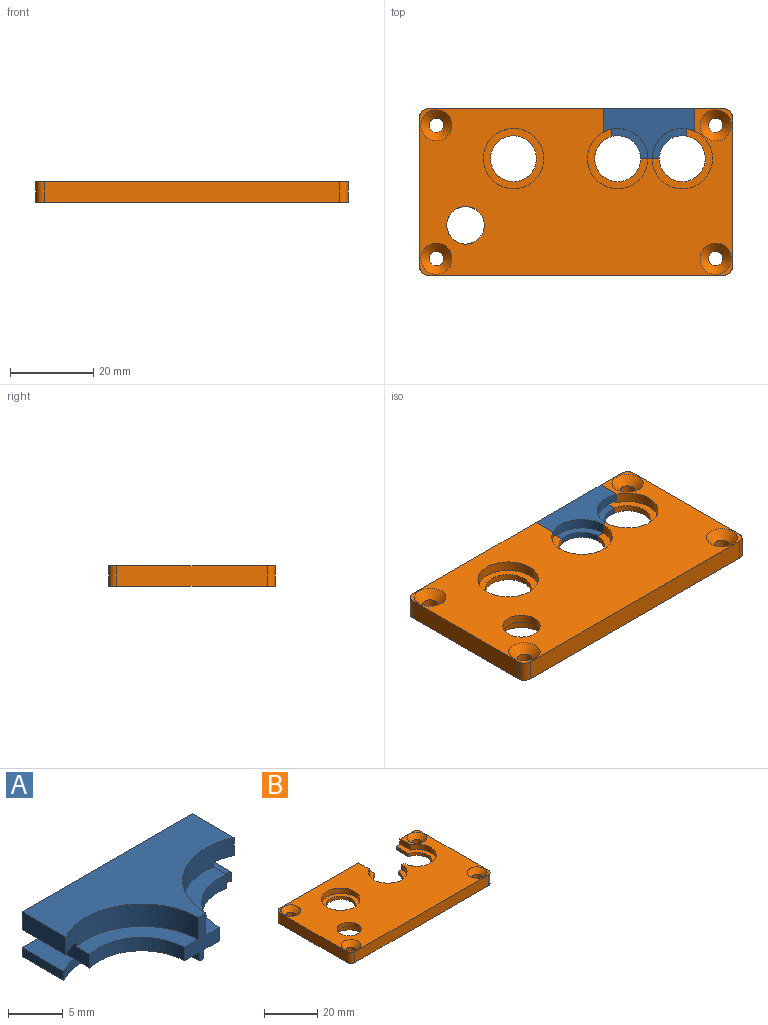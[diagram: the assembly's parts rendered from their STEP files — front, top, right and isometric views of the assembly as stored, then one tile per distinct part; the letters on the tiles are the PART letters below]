
ASSEMBLY  parts=2 mates=1
PART A: 24 faces, bbox 22x12x5 mm
  f0: plane 5x4.5mm, normal (0,-1,0), area 9.7mm2, adj f2,f3,f4,f9,f16,f17,f18,f19
  f1: plane 5.13x1mm, normal (1,0,0), area 5.1mm2, adj f2,f7,f10,f20
  f2: plane 22x12mm, normal (0,0,-1), area 128.5mm2, adj f0,f1,f7,f8,f20,f22
  f3: cylinder r=5.5mm len=6.9mm, axis (0,0,1), area 15.1mm2, adj f0,f15,f17,f23
  f4: cylinder r=5.5mm len=6.4mm, axis (0,0,1), area 14.3mm2, adj f0,f12,f19,f21
  f5: plane 5.65x2mm, normal (-1,0,0), area 11.3mm2, adj f7,f9,f14,f16
  f6: plane 5.4x2mm, normal (1,0,0), area 10.8mm2, adj f7,f9,f11,f18
  f7: plane 22x5mm, normal (0,1,0), area 101.6mm2, adj f1,f2,f5,f6,f8,f9,f10,f11
  f8: plane 5.37x1mm, normal (-1,0,0), area 5.4mm2, adj f2,f7,f13,f22
  f9: plane 22x12mm, normal (0,0,1), area 136mm2, adj f0,f5,f6,f7,f16,f18
  f10: plane 5.13x2.1mm, normal (0,0,1), area 10mm2, adj f1,f7,f12,f20
  f11: plane 5.4x2.1mm, normal (0,0,-1), area 10.6mm2, adj f6,f7,f12,f18
  f12: plane 6.57x2mm, normal (1,0,0), area 12.3mm2, adj f4,f7,f10,f11,f18,f19,f21
  f13: plane 5.37x2.1mm, normal (0,0,1), area 10.4mm2, adj f7,f8,f15,f22
  f14: plane 5.65x2.1mm, normal (0,0,-1), area 10.9mm2, adj f5,f7,f15,f16
  f15: plane 6.68x2mm, normal (-1,0,0), area 12.5mm2, adj f3,f7,f13,f14,f16,f17,f23
  f16: cylinder r=7.25mm len=10.75mm, axis (0,0,1), area 36.5mm2, adj f0,f5,f9,f14,f15,f17
  f17: plane 8.65x7.25mm, normal (0,0,1), area 20mm2, adj f0,f3,f15,f16
  f18: cylinder r=7.25mm len=10.25mm, axis (0,0,1), area 35.1mm2, adj f0,f6,f9,f11,f12,f19
  f19: plane 8.15x7.25mm, normal (0,0,1), area 19.1mm2, adj f0,f4,f12,f18
  f20: cylinder r=7.5mm len=10.5mm, axis (0,0,-1), area 14.9mm2, adj f0,f1,f2,f10,f21
  f21: plane 8.4x7.5mm, normal (0,0,-1), area 22.2mm2, adj f0,f4,f12,f20
  f22: cylinder r=7.5mm len=11mm, axis (0,0,-1), area 15.4mm2, adj f0,f2,f8,f13,f23
  f23: plane 8.9x7.5mm, normal (0,0,-1), area 23.2mm2, adj f0,f3,f15,f22
PART B: 44 faces, bbox 75x40x5 mm
  f0: plane 6.59x1.5mm, normal (-1,0,0), area 9.9mm2, adj f5,f6,f27,f38
  f1: plane 5.4x2.5mm, normal (-1,0,0), area 13.5mm2, adj f5,f17,f27,f28
  f2: plane 5.13x1mm, normal (-1,0,0), area 5.1mm2, adj f5,f18,f37,f38
  f3: plane 5.37x1mm, normal (1,0,0), area 5.4mm2, adj f13,f18,f35,f36
  f4: plane 5.65x2.5mm, normal (1,0,0), area 14.1mm2, adj f13,f17,f29,f30
  f5: plane 9x5mm, normal (0,1,0), area 38mm2, adj f0,f1,f2,f12,f17,f18,f27,f38
  f6: cylinder r=5.5mm len=11mm, axis (0,0,1), area 37.4mm2, adj f0,f27,f38,f42
  f7: cylinder r=5.5mm len=11mm, axis (0,0,1), area 36.6mm2, adj f29,f36,f42,f43
  f8: cylinder r=5.5mm len=11mm, axis (0,0,1), area 51.8mm2, adj f31,f34
  f9: plane 71x5mm, normal (0,-1,0), area 355mm2, adj f10,f16,f17,f18
  f10: cylinder r=2mm len=5mm, axis (0,0,1), area 15.7mm2, adj f9,f11,f17,f18
  f11: plane 36x5mm, normal (1,0,0), area 180mm2, adj f10,f12,f17,f18
  f12: cylinder r=2mm len=5mm, axis (0,0,1), area 15.7mm2, adj f5,f11,f17,f18
  f13: plane 44x5mm, normal (0,1,0), area 213mm2, adj f3,f4,f14,f17,f18,f29,f36,f43
  f14: cylinder r=2mm len=5mm, axis (0,0,1), area 15.7mm2, adj f13,f15,f17,f18
  f15: plane 36x5mm, normal (-1,0,0), area 180mm2, adj f14,f16,f17,f18
  f16: cylinder r=2mm len=5mm, axis (0,0,1), area 15.7mm2, adj f9,f15,f17,f18
  f17: plane 75x40mm, normal (0,0,1), area 2124.9mm2, adj f1,f4,f5,f9,f10,f11,f12,f13
  f18: plane 75x40mm, normal (0,0,-1), area 2166.7mm2, adj f2,f3,f5,f9,f10,f11,f12,f13
  f19: cylinder r=1.75mm len=3.5mm, axis (0,0,1), area 33mm2, adj f18,f26
  f20: cylinder r=1.75mm len=3.5mm, axis (0,0,1), area 33mm2, adj f18,f25
  f21: cylinder r=1.75mm len=3.5mm, axis (0,0,1), area 33mm2, adj f18,f24
  f22: cylinder r=1.75mm len=3.5mm, axis (0,0,1), area 33mm2, adj f18,f23
  f23: cone r=1.75mm half-angle=45deg, axis (0,0,1), area 48.9mm2, adj f17,f22
  f24: cone r=1.75mm half-angle=45deg, axis (0,0,1), area 48.9mm2, adj f17,f21
  f25: cone r=1.75mm half-angle=45deg, axis (0,0,1), area 48.9mm2, adj f17,f20
  f26: cone r=1.75mm half-angle=45deg, axis (0,0,1), area 48.9mm2, adj f17,f19
  f27: plane 19.25x14.5mm, normal (0,0,1), area 60.9mm2, adj f0,f1,f5,f6,f28,f42
  f28: cylinder r=7.25mm len=14.5mm, axis (0,0,1), area 77.7mm2, adj f1,f17,f27,f42
  f29: plane 19.25x14.5mm, normal (0,0,1), area 60.4mm2, adj f4,f7,f13,f30,f42,f43
  f30: cylinder r=7.25mm len=14.5mm, axis (0,0,1), area 76.3mm2, adj f4,f17,f29,f42
  f31: plane 14.5x14.5mm, normal (0,0,1), area 70.1mm2, adj f8,f32
  f32: cylinder r=7.25mm len=14.5mm, axis (0,0,1), area 113.9mm2, adj f17,f31
  f33: cylinder r=7.5mm len=15mm, axis (0,0,-1), area 47.1mm2, adj f18,f34
  f34: plane 15x15mm, normal (0,0,-1), area 81.7mm2, adj f8,f33
  f35: cylinder r=7.5mm len=15mm, axis (0,0,-1), area 31.7mm2, adj f3,f18,f36,f42
  f36: plane 19.5x15mm, normal (0,0,-1), area 68.1mm2, adj f3,f7,f13,f35,f42,f43
  f37: cylinder r=7.5mm len=15mm, axis (0,0,-1), area 32.3mm2, adj f2,f18,f38,f42
  f38: plane 19.5x15mm, normal (0,0,-1), area 68.8mm2, adj f0,f2,f5,f6,f37,f42
  f39: cylinder r=4.5mm len=9mm, axis (0,0,-1), area 56.5mm2, adj f17,f40
  f40: plane 13x13mm, normal (0,0,-1), area 69.1mm2, adj f39,f41
  f41: cylinder r=6.5mm len=13mm, axis (0,0,-1), area 122.5mm2, adj f18,f40
  f42: plane 5x4.5mm, normal (0,1,0), area 9.8mm2, adj f6,f7,f17,f18,f27,f28,f29,f30
  f43: plane 6.71x1.5mm, normal (1,0,0), area 10.1mm2, adj f7,f13,f29,f36
PLACE A t=(18.59,16.46,0)mm
PLACE B t=(1.09,2.46,0)mm
MATE fastened A.f7 <-> B.f13  axis (0,1,0) through (9.69,22.46,1)mm
